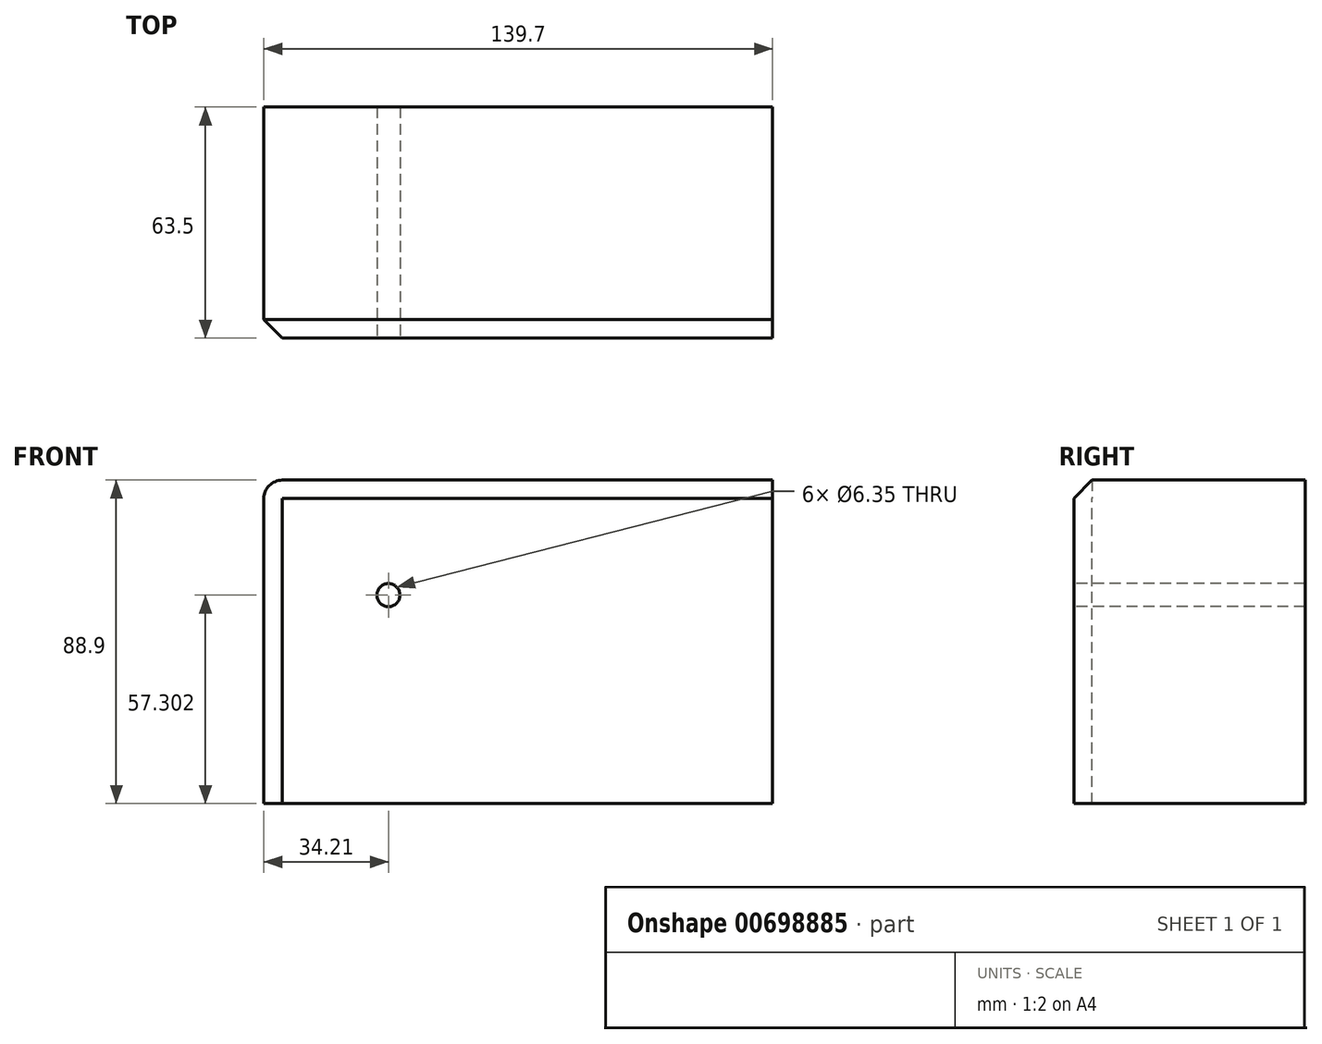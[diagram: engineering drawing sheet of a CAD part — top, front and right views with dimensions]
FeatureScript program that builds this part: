
annotation { "Feature Type Name" : "Feature", "Feature Type Description" : "" }
export const myFeature = defineFeature(function(context is Context, id is Id, definition is map)
    precondition{}
    {
        {
            var Q0;
            Q0=qCreatedBy(makeId("Front.planeOp"),FACE);
            var sketch = newSketch(context, id + "F0", { "sketchPlane" : qUnion([Q0])});
            skLineSegment(sketch, "E0.bottom", {"start": v(-66.82, 41.42) * mm, "end": v(72.88, 41.42) * mm});
            skLineSegment(sketch, "E0.top", {"start": v(-66.82, -47.48) * mm, "end": v(72.88, -47.48) * mm});
            skLineSegment(sketch, "E0.left", {"start": v(-66.82, 41.42) * mm, "end": v(-66.82, -47.48) * mm});
            skLineSegment(sketch, "E0.right", {"start": v(72.88, 41.42) * mm, "end": v(72.88, -47.48) * mm});
            skSolve(sketch);
        }
        {
            var Q0;
            Q0=makeQuery(id+"F0.imprint","IMPRINT",FACE,{"disambiguationData":[TD([[makeQuery(id+"F0.imprint","IMPRINT",EDGE,{"derivedFrom":sQuery(id+"F0.wireOp",EDGE,"E0.bottom")}),-1.0]])]});
            extrude(context, id + "F1", {"entities" : qUnion([Q0]), "depth" : 63.5 * mm, "offsetDistance" : 25.4 * mm});
        }
        {
            var Q0;
            Q0=makeQuery(id+"F1.opExtrude","SWEPT_EDGE",EDGE,{"disambiguationData":[OSD([sQuery(id+"F0.wireOp",EDGE,"E0.bottom"),sQuery(id+"F0.wireOp",EDGE,"E0.left")])]});
            fillet(context, id + "F2", {"entities" : qUnion([Q0]), "radius" : 5.08 * mm, "tangentPropagation" : true, "allowEdgeOverflow" : false});
        }
        {
            var Q0;
            Q0=makeQuery(id+"F1.opExtrude","CAP_EDGE",EDGE,{"disambiguationData":[OSD([sQuery(id+"F0.wireOp",EDGE,"E0.bottom")])],"isStart":false});
            chamfer(context, id + "F3", {"entities" : qUnion([Q0]), "width" : 5.08 * mm, "tangentPropagation" : true});
        }
        {
            var Q0;
            Q0=makeQuery(id+"F1.opExtrude","CAP_FACE",FACE,{"disambiguationData":[OSD([sQuery(id+"F0.wireOp",EDGE,"E0.bottom"),sQuery(id+"F0.wireOp",EDGE,"E0.top"),sQuery(id+"F0.wireOp",EDGE,"E0.left"),sQuery(id+"F0.wireOp",EDGE,"E0.right")])],"isStart":false});
            var sketch = newSketch(context, id + "F4", { "sketchPlane" : qUnion([Q0])});
            skPoint(sketch, "E1", {"position": v(-32.6, 9.82) * mm});
            skSolve(sketch);
        }
        {
            var Q0;
            Q0=sQuery(id+"F4.wireOp",VERTEX,"E1");
            var Q1;
            Q1=makeQuery(id+"F1.opExtrude","SWEPT_BODY",BODY,{"disambiguationData":[OSD([sQuery(id+"F0.wireOp",EDGE,"E0.bottom"),sQuery(id+"F0.wireOp",EDGE,"E0.top"),sQuery(id+"F0.wireOp",EDGE,"E0.left"),sQuery(id+"F0.wireOp",EDGE,"E0.right")])]});
            hole(context, id + "F5", {"style" : HoleStyle.SIMPLE, "endStyle" : HoleEndStyle.THROUGH, "holeDiameter" : 6.35 * mm, "majorDiameter" : 6.35 * mm, "isTappedThrough" : true, "tappedDepth" : 12.7 * mm, "tapClearance" : 3, "locations" : qUnion([Q0]), "scope" : qUnion([Q1])});
        }
    });
